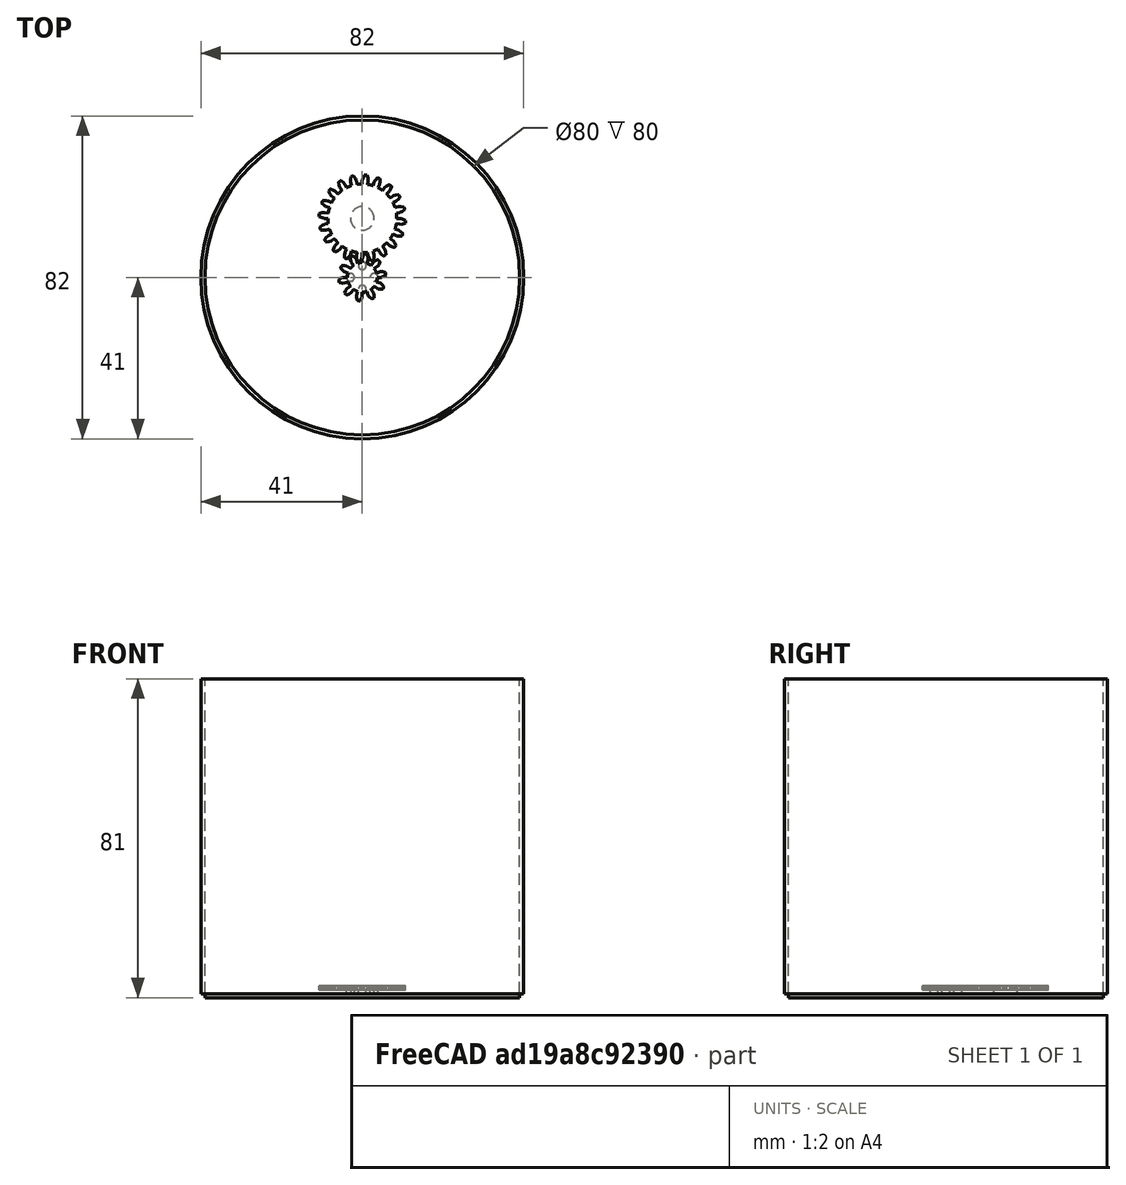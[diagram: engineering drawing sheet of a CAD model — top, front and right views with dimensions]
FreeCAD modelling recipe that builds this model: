
FCSTD DOCUMENT  (FreeCAD 0.14R2935 (Git))
Label: base-static-00
License: CC-BY 3.0
LicenseURL: http://creativecommons.org/licenses/by/3.0/
objects: Part::Cylinder×8, Part::FeaturePython×2, Part::Fillet×1, Part::Cut×1, App::DocumentObjectGroup×1
note: 12 computed .brp shape members not serialized (recipe doc carries the construction recipe); baked Part::Feature solids carry a one-line shape summary decoded from their .brp

FEATURE [Part::Cylinder] Cylinder
  Angle = 360
  Height = 1
  Radius = 40
FEATURE [Part::Cylinder] Cylinder001
  Angle = 360
  Height = 1
  Placement = pos=(0,3,1) rot=(0,0,1;0rad)
  Radius = 1
FEATURE [Part::FeaturePython] Gear  # WARN: FeaturePython — macro-defined, semantics opaque (R4)
  CenterRadius = 0
  GearHeight = 1
  LevelOfDetail = 3
  Module = 1
  NumberTeeth = 10
  Placement = pos=(0,0,2) rot=(0,0,1;0rad)
  PressureAngle = 15
  Verbose = true
FEATURE [Part::FeaturePython] Gear001  # WARN: FeaturePython — macro-defined, semantics opaque (R4)
  CenterRadius = 0
  GearHeight = 1
  LevelOfDetail = 3
  Module = 1
  NumberTeeth = 20
  Placement = pos=(0,15,2) rot=(0,0,-1;0.15708rad)
  PressureAngle = 15
  Verbose = true
FEATURE [Part::Cylinder] Cylinder002
  Angle = 360
  Height = 1
  Placement = pos=(0,-3,1) rot=(0,0,1;0rad)
  Radius = 1
FEATURE [Part::Cylinder] Cylinder003
  Angle = 360
  Height = 1
  Placement = pos=(3,0,1) rot=(0,0,1;0rad)
  Radius = 1
FEATURE [Part::Cylinder] Cylinder004
  Angle = 360
  Height = 1
  Placement = pos=(-3,0,1) rot=(0,0,1;0rad)
  Radius = 1
FEATURE [Part::Cylinder] Cylinder005
  Angle = 360
  Height = 1
  Placement = pos=(0,15,1) rot=(0,0,1;0rad)
  Radius = 3
FEATURE [Part::Fillet] Fillet
  Base = -> Cylinder005
  Edges = 1 edges r=0.7: [Edge3]
FEATURE [Part::Cylinder] Cylinder006
  Angle = 360
  Height = 80
  Placement = pos=(0,0,1) rot=(0,0,1;0rad)
  Radius = 40
FEATURE [Part::Cylinder] Cylinder007
  Angle = 360
  Height = 80
  Placement = pos=(0,0,1) rot=(0,0,1;0rad)
  Radius = 41
FEATURE [Part::Cut] Cut
  Base = -> Cylinder007
  Tool = -> Cylinder006
FEATURE [App::DocumentObjectGroup] Group  label="bottom"
  Group = -> [Cylinder,Cylinder001,Gear,Gear001,Cylinder002,Cylinder003,Cylinder004,Fillet,Cut]
